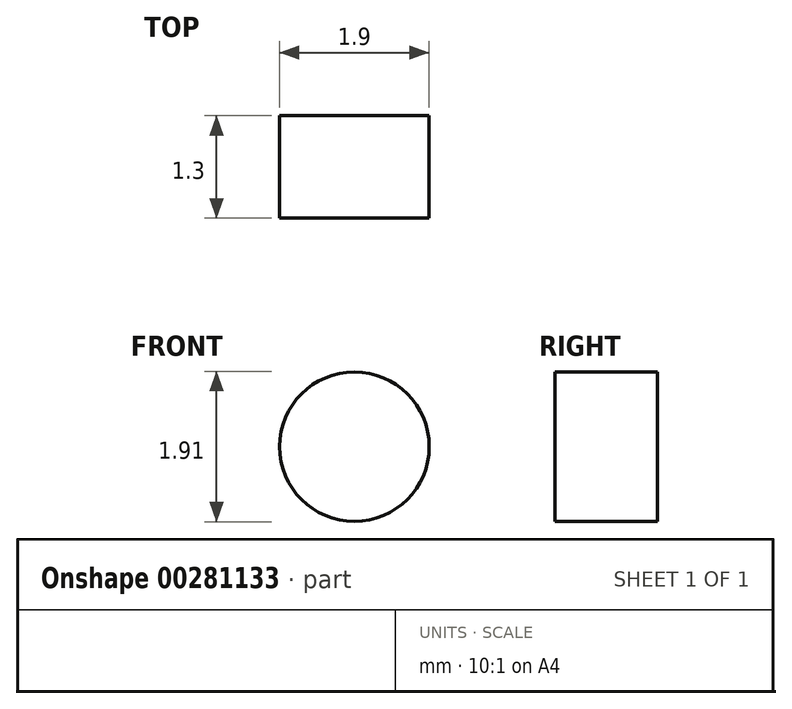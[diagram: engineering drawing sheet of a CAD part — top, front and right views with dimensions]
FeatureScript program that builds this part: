
annotation { "Feature Type Name" : "Feature", "Feature Type Description" : "" }
export const myFeature = defineFeature(function(context is Context, id is Id, definition is map)
    precondition{}
    {
        {
            var Q0;
            Q0=qCreatedBy(makeId("Front.planeOp"),FACE);
            var sketch = newSketch(context, id + "F0", { "sketchPlane" : qUnion([Q0])});
            skCircle(sketch, "E0", {"center": v(-5.02, -18.16) * mm, "radius": 0.95 * mm});
            skCircle(sketch, "E1", {"center": v(5.02, -18.16) * mm, "radius": 0.95 * mm});
            skArc(sketch, "E2", {"start": v(2.63, -16.24) * mm, "mid": v(0, 16.45) * mm, "end": v(-2.63, -16.24) * mm});
            skLineSegment(sketch, "E3", {"start": v(-2.63, -20.15) * mm, "end": v(-2.63, -16.24) * mm});
            skLineSegment(sketch, "E4", {"start": v(-7.1, -20.15) * mm, "end": v(-2.63, -20.15) * mm});
            skLineSegment(sketch, "E5", {"start": v(-10.64, -15.2) * mm, "end": v(-7.1, -20.15) * mm});
            skArc(sketch, "E6", {"start": v(0, 20.35) * mm, "mid": v(-18.72, 6.59) * mm, "end": v(-10.64, -15.2) * mm});
            skArc(sketch, "E7", {"start": v(10.64, -15.2) * mm, "mid": v(18.72, 6.59) * mm, "end": v(0, 20.35) * mm});
            skLineSegment(sketch, "E8", {"start": v(10.64, -15.2) * mm, "end": v(7.1, -20.15) * mm});
            skLineSegment(sketch, "E9", {"start": v(7.1, -20.15) * mm, "end": v(2.63, -20.15) * mm});
            skLineSegment(sketch, "E10", {"start": v(2.63, -20.15) * mm, "end": v(2.63, -16.24) * mm});
            skCircle(sketch, "E11", {"center": v(0, 0) * mm, "radius": 16.45 * mm, "construction": true});
            skSolve(sketch);
        }
        {
            var Q0;
            Q0=makeQuery(id+"F0.imprint","IMPRINT",FACE,{"disambiguationData":[TD([[makeQuery(id+"F0.imprint","IMPRINT",EDGE,{"derivedFrom":sQuery(id+"F0.wireOp",EDGE,"E0")}),1.0]])]});
            extrude(context, id + "F1", {"entities" : qUnion([Q0]), "depth" : 1.3 * mm});
        }
    });
